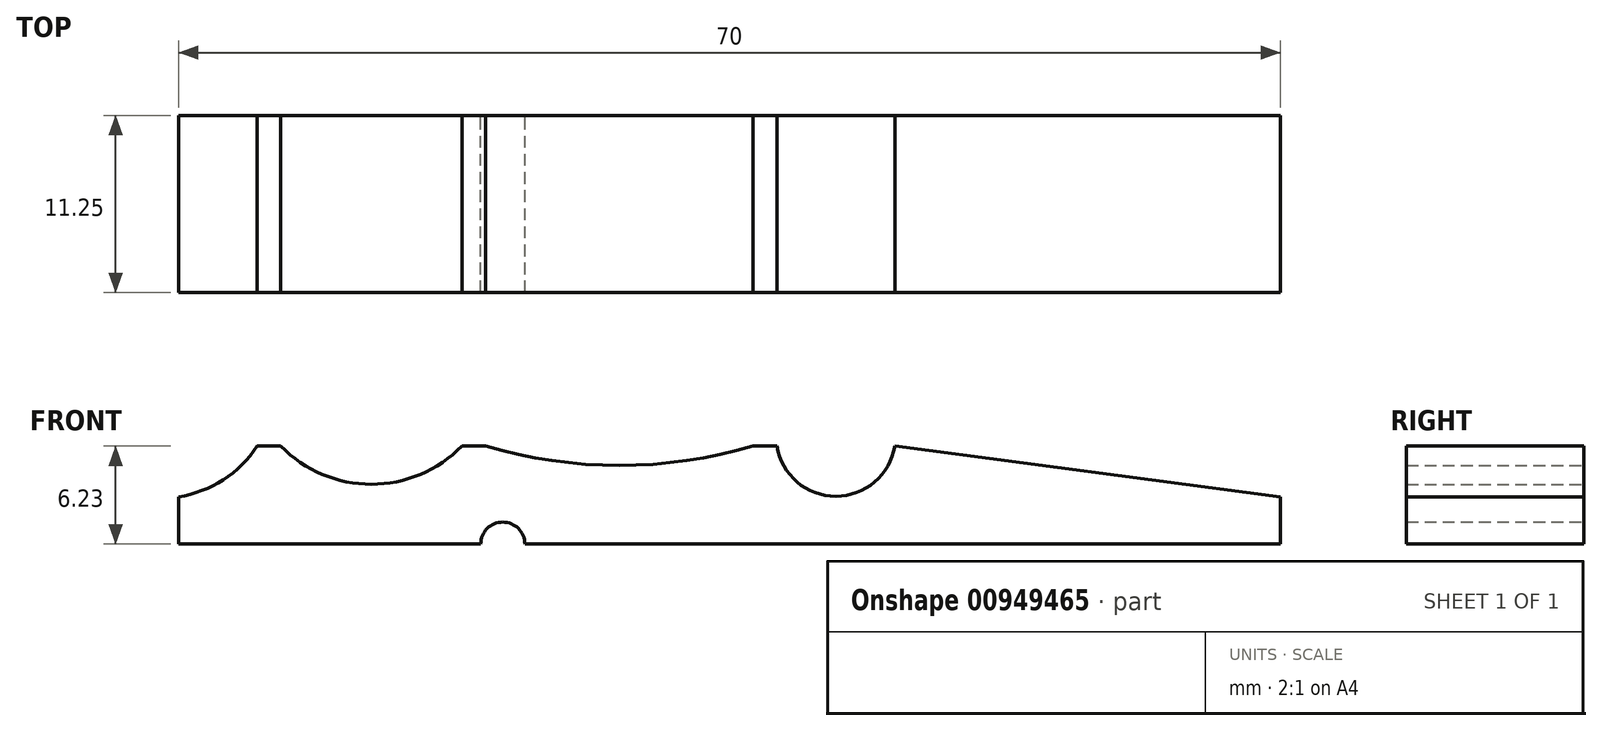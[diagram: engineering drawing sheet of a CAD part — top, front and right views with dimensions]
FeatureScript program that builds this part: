
annotation { "Feature Type Name" : "Feature", "Feature Type Description" : "" }
export const myFeature = defineFeature(function(context is Context, id is Id, definition is map)
    precondition{}
    {
        {
            var Q0;
            Q0=qCreatedBy(makeId("Front.planeOp"),FACE);
            var sketch = newSketch(context, id + "F0", { "sketchPlane" : qUnion([Q0])});
            skLineSegment(sketch, "E0.top", {"start": v(-84.17, 7.43) * mm, "end": v(-14.17, 7.43) * mm, "construction": true});
            skLineSegment(sketch, "E0.left", {"start": v(-84.17, 10.43) * mm, "end": v(-84.17, 7.43) * mm});
            skLineSegment(sketch, "E0.right", {"start": v(-14.17, 10.43) * mm, "end": v(-14.17, 7.43) * mm});
            skLineSegment(sketch, "E1", {"start": v(-91.89, 13.66) * mm, "end": v(-12.1, 13.66) * mm, "construction": true});
            skArc(sketch, "E2", {"start": v(-84.17, 10.43) * mm, "mid": v(-81.33, 11.52) * mm, "end": v(-79.17, 13.66) * mm});
            skArc(sketch, "E3", {"start": v(-64.67, 13.66) * mm, "mid": v(-56.17, 12.43) * mm, "end": v(-47.67, 13.66) * mm});
            skLineSegment(sketch, "E4", {"start": v(-38.67, 13.66) * mm, "end": v(-14.17, 10.43) * mm});
            skLineSegment(sketch, "E5", {"start": v(-79.17, 13.66) * mm, "end": v(-77.67, 13.66) * mm});
            skLineSegment(sketch, "E6", {"start": v(-64.67, 13.66) * mm, "end": v(-66.17, 13.66) * mm});
            skLineSegment(sketch, "E7", {"start": v(-47.67, 13.66) * mm, "end": v(-46.17, 13.66) * mm});
            skArc(sketch, "E8", {"start": v(-77.67, 13.66) * mm, "mid": v(-71.92, 11.23) * mm, "end": v(-66.17, 13.66) * mm});
            skArc(sketch, "E9", {"start": v(-46.17, 13.66) * mm, "mid": v(-42.42, 10.47) * mm, "end": v(-38.67, 13.66) * mm});
            skLineSegment(sketch, "E10", {"start": v(-84.17, 7.43) * mm, "end": v(-64.97, 7.43) * mm});
            skLineSegment(sketch, "E11", {"start": v(-14.17, 7.43) * mm, "end": v(-62.17, 7.43) * mm});
            skArc(sketch, "E12", {"start": v(-62.17, 7.43) * mm, "mid": v(-63.57, 8.83) * mm, "end": v(-64.97, 7.43) * mm});
            skSolve(sketch);
        }
        {
            var Q0;
            Q0 = qSketchRegion(id + "F0", true);
            extrude(context, id + "F1", {"entities" : qUnion([Q0]), "depth" : 11.25 * mm, "offsetDistance" : 25 * mm});
        }
    });
